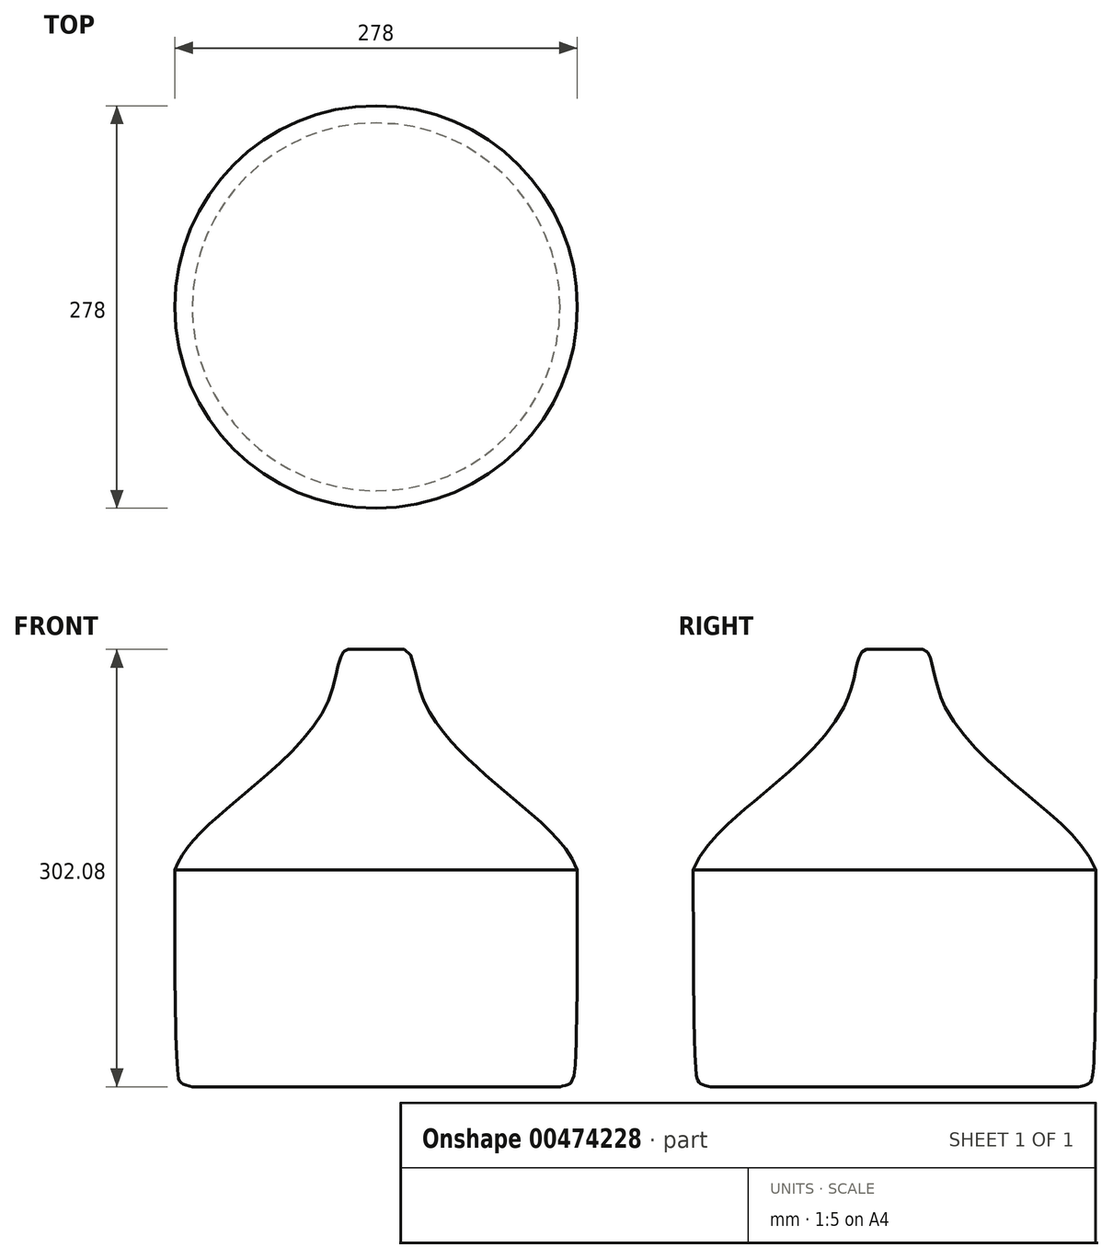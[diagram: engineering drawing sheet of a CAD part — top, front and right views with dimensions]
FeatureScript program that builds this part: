
annotation { "Feature Type Name" : "Feature", "Feature Type Description" : "" }
export const myFeature = defineFeature(function(context is Context, id is Id, definition is map)
    precondition{}
    {
        {
            var Q0;
            Q0=qCreatedBy(makeId("Front.planeOp"),FACE);
            var sketch = newSketch(context, id + "F0", { "sketchPlane" : qUnion([Q0])});
            skLineSegment(sketch, "E0", {"start": v(0, 0) * mm, "end": v(127, 0) * mm});
            skFitSpline(sketch, "E1", {"points": [v(127, 0) * mm, v(134.22, 2.35) * mm, v(136.86, 8.81) * mm, v(139, 149.77) * mm], "startDerivative": vector(52.21, 11.42) * mm, "endDerivative": vector(0.05, 270.33) * mm});
            skFitSpline(sketch, "E2", {"points": [v(139, 149.77) * mm, v(112.8, 183.5) * mm, v(33.74, 264.78) * mm, v(19.37, 302.08) * mm], "startDerivative": vector(-49.03, 118.36) * mm, "endDerivative": vector(-83.74, 0) * mm});
            skLineSegment(sketch, "E3", {"start": v(19.37, 302.08) * mm, "end": v(0, 302.08) * mm});
            skLineSegment(sketch, "E4", {"start": v(0, 302.08) * mm, "end": v(0, 0) * mm, "construction": true});
            skLineSegment(sketch, "E5", {"start": v(0, 302.08) * mm, "end": v(0, 292.76) * mm});
            skLineSegment(sketch, "E6", {"start": v(0, 292.76) * mm, "end": v(15.47, 292.76) * mm});
            skLineSegment(sketch, "E7", {"start": v(15.47, 292.76) * mm, "end": v(34.41, 247.54) * mm});
            skLineSegment(sketch, "E8", {"start": v(34.41, 247.54) * mm, "end": v(118.27, 170.54) * mm});
            skLineSegment(sketch, "E9", {"start": v(118.27, 170.54) * mm, "end": v(129.42, 147.9) * mm});
            skLineSegment(sketch, "E10", {"start": v(129.42, 147.9) * mm, "end": v(129.42, 9.62) * mm});
            skLineSegment(sketch, "E11", {"start": v(129.42, 9.62) * mm, "end": v(0, 9.62) * mm});
            skLineSegment(sketch, "E12", {"start": v(0, 9.62) * mm, "end": v(0, 0) * mm});
            skSolve(sketch);
        }
        {
            var Q0;
            Q0=sQuery(id+"F0.wireOp",EDGE,"E3");
            var Q1;
            Q1=sQuery(id+"F0.wireOp",EDGE,"E2");
            var Q2;
            Q2=sQuery(id+"F0.wireOp",EDGE,"E1");
            var Q3;
            Q3=sQuery(id+"F0.wireOp",EDGE,"E0");
            var Q4;
            Q4=sQuery(id+"F0.wireOp",EDGE,"E4");
            revolve(context, id + "F1", {"bodyType" : ToolBodyType.SURFACE, "surfaceEntities" : qUnion([Q0, Q1, Q2, Q3]), "axis" : qUnion([Q4]), "revolveType" : RevolveType.FULL});
        }
    });
